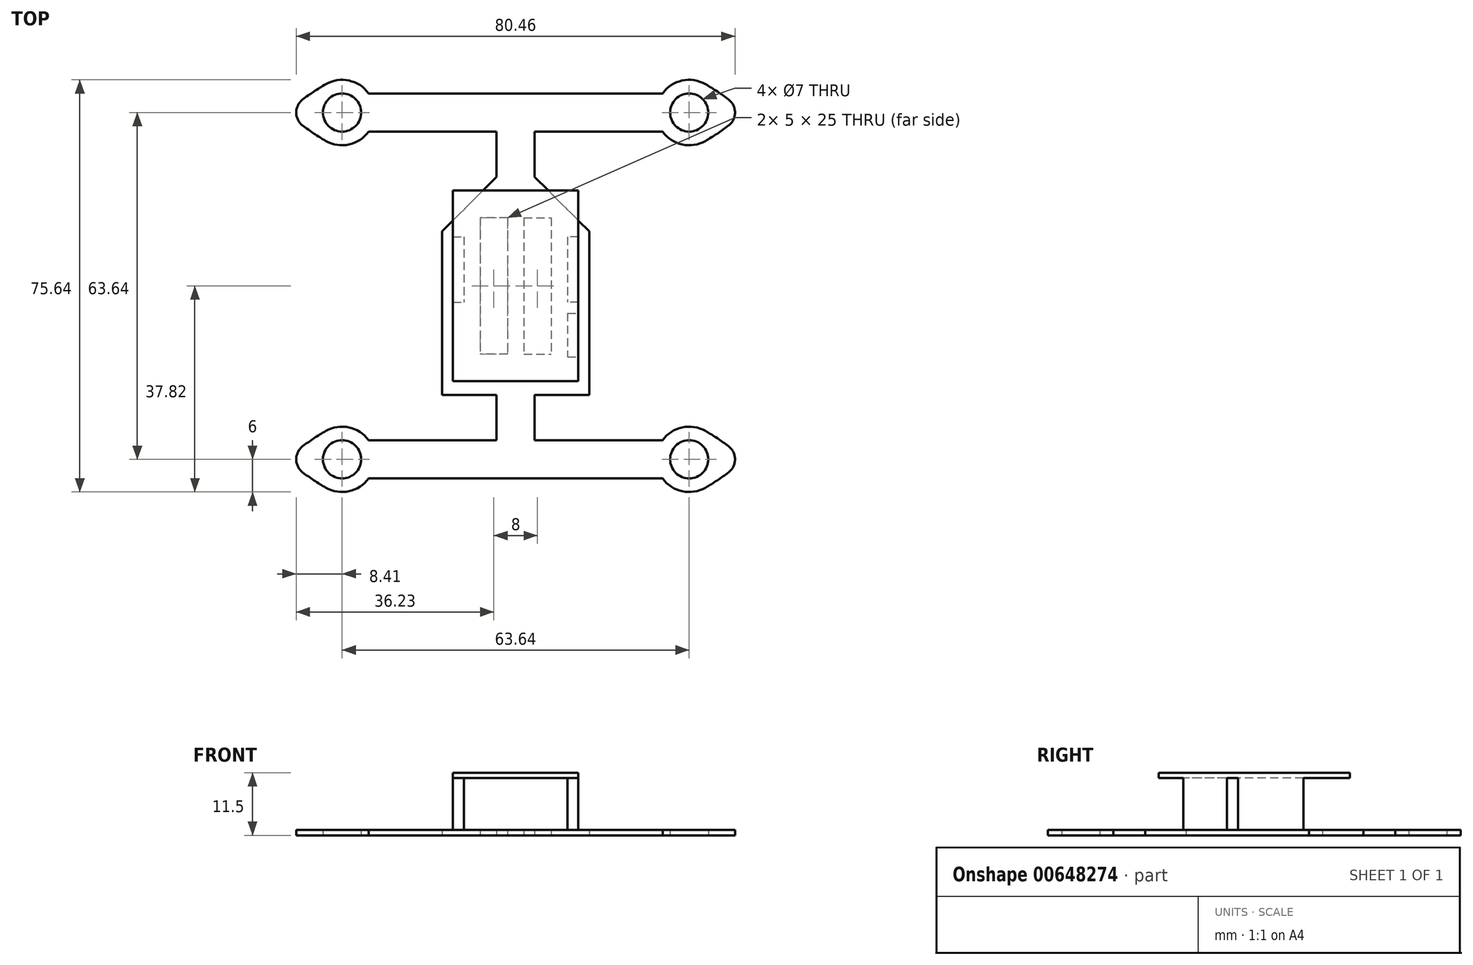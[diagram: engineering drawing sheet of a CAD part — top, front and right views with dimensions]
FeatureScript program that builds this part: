
annotation { "Feature Type Name" : "Feature", "Feature Type Description" : "" }
export const myFeature = defineFeature(function(context is Context, id is Id, definition is map)
    precondition{}
    {
        {
            var Q0;
            Q0=qCreatedBy(makeId("Top.planeOp"),FACE);
            var sketch = newSketch(context, id + "F0", { "sketchPlane" : qUnion([Q0])});
            skLineSegment(sketch, "E0.bottom", {"start": v(31.82, -31.82) * mm, "end": v(-31.82, -31.82) * mm, "construction": true});
            skLineSegment(sketch, "E0.top", {"start": v(31.82, 31.82) * mm, "end": v(-31.82, 31.82) * mm, "construction": true});
            skLineSegment(sketch, "E0.left", {"start": v(31.82, -31.82) * mm, "end": v(31.82, 31.82) * mm, "construction": true});
            skLineSegment(sketch, "E0.right", {"start": v(-31.82, -31.82) * mm, "end": v(-31.82, 31.82) * mm, "construction": true});
            skCircle(sketch, "E1", {"center": v(-31.82, 31.82) * mm, "radius": 3.5 * mm});
            skCircle(sketch, "E2", {"center": v(31.82, 31.82) * mm, "radius": 3.5 * mm});
            skCircle(sketch, "E3", {"center": v(31.82, -31.82) * mm, "radius": 3.5 * mm});
            skCircle(sketch, "E4", {"center": v(-31.82, -31.82) * mm, "radius": 3.5 * mm});
            skCircle(sketch, "E5", {"center": v(-31.82, 31.82) * mm, "radius": 6 * mm});
            skCircle(sketch, "E6", {"center": v(31.82, 31.82) * mm, "radius": 6 * mm});
            skCircle(sketch, "E7", {"center": v(31.82, -31.82) * mm, "radius": 6 * mm});
            skCircle(sketch, "E8", {"center": v(-31.82, -31.82) * mm, "radius": 6 * mm});
            skLineSegment(sketch, "E9", {"start": v(-26.95, 35.32) * mm, "end": v(26.95, 35.32) * mm});
            skLineSegment(sketch, "E10.0", {"start": v(-26.95, 28.32) * mm, "end": v(-3.5, 28.32) * mm});
            skLineSegment(sketch, "E11.0", {"start": v(3.5, 20) * mm, "end": v(3.5, 28.32) * mm});
            skLineSegment(sketch, "E12.0", {"start": v(-3.5, 20) * mm, "end": v(-3.5, 28.32) * mm});
            skLineSegment(sketch, "E13", {"start": v(3.5, 28.32) * mm, "end": v(26.95, 28.32) * mm});
            skLineSegment(sketch, "E14.MirrorCS", {"start": v(3.5, -20) * mm, "end": v(3.5, -28.32) * mm});
            skLineSegment(sketch, "E15.MirrorCS", {"start": v(-3.5, -20) * mm, "end": v(-3.5, -28.32) * mm});
            skLineSegment(sketch, "E16.MirrorCS", {"start": v(3.5, -28.32) * mm, "end": v(26.95, -28.32) * mm});
            skLineSegment(sketch, "E17.MirrorCS", {"start": v(-26.95, -35.32) * mm, "end": v(26.95, -35.32) * mm});
            skLineSegment(sketch, "E18.MirrorCS", {"start": v(-26.95, -28.32) * mm, "end": v(-3.5, -28.32) * mm});
            skArc(sketch, "E19", {"start": v(39.04, 34.2) * mm, "mid": v(36.98, 35.68) * mm, "end": v(34.82, 37.02) * mm});
            skArc(sketch, "E20", {"start": v(34.82, 26.62) * mm, "mid": v(36.98, 27.96) * mm, "end": v(39.04, 29.43) * mm});
            skPoint(sketch, "E21.visualSharp", {"position": v(41.9, 31.82) * mm});
            skArc(sketch, "E21.filletArc", {"start": v(39.04, 29.43) * mm, "mid": v(40.23, 31.82) * mm, "end": v(39.04, 34.2) * mm});
            skArc(sketch, "E22.MirrorCS", {"start": v(-34.82, 26.62) * mm, "mid": v(-36.98, 27.96) * mm, "end": v(-39.04, 29.43) * mm});
            skArc(sketch, "E23.MirrorCS", {"start": v(-39.04, 29.43) * mm, "mid": v(-40.23, 31.82) * mm, "end": v(-39.04, 34.2) * mm});
            skArc(sketch, "E24.MirrorCS", {"start": v(-39.04, 34.2) * mm, "mid": v(-36.98, 35.68) * mm, "end": v(-34.82, 37.02) * mm});
            skArc(sketch, "E25.MirrorCS", {"start": v(-34.82, -26.62) * mm, "mid": v(-36.98, -27.96) * mm, "end": v(-39.04, -29.43) * mm});
            skArc(sketch, "E26.MirrorCS", {"start": v(-39.04, -29.43) * mm, "mid": v(-40.23, -31.82) * mm, "end": v(-39.04, -34.2) * mm});
            skArc(sketch, "E27.MirrorCS", {"start": v(-39.04, -34.2) * mm, "mid": v(-36.98, -35.68) * mm, "end": v(-34.82, -37.02) * mm});
            skArc(sketch, "E28.MirrorCS", {"start": v(34.82, -26.62) * mm, "mid": v(36.98, -27.96) * mm, "end": v(39.04, -29.43) * mm});
            skArc(sketch, "E29.MirrorCS", {"start": v(39.04, -29.43) * mm, "mid": v(40.23, -31.82) * mm, "end": v(39.04, -34.2) * mm});
            skArc(sketch, "E30.MirrorCS", {"start": v(39.04, -34.2) * mm, "mid": v(36.98, -35.68) * mm, "end": v(34.82, -37.02) * mm});
            skLineSegment(sketch, "E31", {"start": v(0, 75.71) * mm, "end": v(0, -73.85) * mm, "construction": true});
            skLineSegment(sketch, "E32", {"start": v(-74.14, 0) * mm, "end": v(71.7, 0) * mm, "construction": true});
            skLineSegment(sketch, "E33.bottom", {"start": v(1.5, 12.5) * mm, "end": v(6.5, 12.5) * mm});
            skLineSegment(sketch, "E33.top", {"start": v(1.5, -12.5) * mm, "end": v(6.5, -12.5) * mm});
            skLineSegment(sketch, "E33.left", {"start": v(1.5, 12.5) * mm, "end": v(1.5, -12.5) * mm});
            skLineSegment(sketch, "E33.right", {"start": v(6.5, 12.5) * mm, "end": v(6.5, -12.5) * mm});
            skLineSegment(sketch, "E34.MirrorCS", {"start": v(-1.5, -12.5) * mm, "end": v(-6.5, -12.5) * mm});
            skLineSegment(sketch, "E35.MirrorCS", {"start": v(-1.5, 12.5) * mm, "end": v(-1.5, -12.5) * mm});
            skLineSegment(sketch, "E36.MirrorCS", {"start": v(-6.5, 12.5) * mm, "end": v(-6.5, -12.5) * mm});
            skLineSegment(sketch, "E37.MirrorCS", {"start": v(-1.5, 12.5) * mm, "end": v(-6.5, 12.5) * mm});
            skLineSegment(sketch, "E38", {"start": v(-3.5, 20) * mm, "end": v(-13.5, 10) * mm});
            skLineSegment(sketch, "E39", {"start": v(-13.5, 10) * mm, "end": v(-13.5, -20) * mm});
            skLineSegment(sketch, "E40.MirrorCS", {"start": v(3.5, 20) * mm, "end": v(13.5, 10) * mm});
            skLineSegment(sketch, "E41", {"start": v(13.5, 10) * mm, "end": v(13.5, -20) * mm});
            skLineSegment(sketch, "E42.trimOffspring", {"start": v(-3.5, -20) * mm, "end": v(-13.5, -20) * mm});
            skLineSegment(sketch, "E43", {"start": v(13.5, -20) * mm, "end": v(3.5, -20) * mm});
            skSolve(sketch);
        }
        {
            var Q0;
            Q0 = qSketchRegion(id + "F0", true);
            extrude(context, id + "F1", {"entities" : qUnion([Q0]), "depth" : 1 * mm, "offsetDistance" : 25 * mm});
        }
        {
            var Q0;
            Q0=makeQuery(id+"F1.opExtrude","CAP_FACE",FACE,{"disambiguationData":[OSD([sQuery(id+"F0.wireOp",EDGE,"E1"),sQuery(id+"F0.wireOp",EDGE,"E2"),sQuery(id+"F0.wireOp",EDGE,"E3"),sQuery(id+"F0.wireOp",EDGE,"E4"),sQuery(id+"F0.wireOp",EDGE,"E5"),sQuery(id+"F0.wireOp",EDGE,"E6"),sQuery(id+"F0.wireOp",EDGE,"E7"),sQuery(id+"F0.wireOp",EDGE,"E8"),sQuery(id+"F0.wireOp",EDGE,"E9"),sQuery(id+"F0.wireOp",EDGE,"E10.0"),sQuery(id+"F0.wireOp",EDGE,"E11.0"),sQuery(id+"F0.wireOp",EDGE,"E12.0"),sQuery(id+"F0.wireOp",EDGE,"E13"),sQuery(id+"F0.wireOp",EDGE,"E14.MirrorCS"),sQuery(id+"F0.wireOp",EDGE,"E15.MirrorCS"),sQuery(id+"F0.wireOp",EDGE,"E16.MirrorCS"),sQuery(id+"F0.wireOp",EDGE,"E17.MirrorCS"),sQuery(id+"F0.wireOp",EDGE,"E18.MirrorCS"),sQuery(id+"F0.wireOp",EDGE,"E19"),sQuery(id+"F0.wireOp",EDGE,"E20"),sQuery(id+"F0.wireOp",EDGE,"E21.filletArc"),sQuery(id+"F0.wireOp",EDGE,"E22.MirrorCS"),sQuery(id+"F0.wireOp",EDGE,"E24.MirrorCS"),sQuery(id+"F0.wireOp",EDGE,"E23.MirrorCS"),sQuery(id+"F0.wireOp",EDGE,"E25.MirrorCS"),sQuery(id+"F0.wireOp",EDGE,"E26.MirrorCS"),sQuery(id+"F0.wireOp",EDGE,"E27.MirrorCS"),sQuery(id+"F0.wireOp",EDGE,"E28.MirrorCS"),sQuery(id+"F0.wireOp",EDGE,"E29.MirrorCS"),sQuery(id+"F0.wireOp",EDGE,"E30.MirrorCS"),sQuery(id+"F0.wireOp",EDGE,"E33.bottom"),sQuery(id+"F0.wireOp",EDGE,"E33.top"),sQuery(id+"F0.wireOp",EDGE,"E33.left"),sQuery(id+"F0.wireOp",EDGE,"E33.right"),sQuery(id+"F0.wireOp",EDGE,"E34.MirrorCS"),sQuery(id+"F0.wireOp",EDGE,"E35.MirrorCS"),sQuery(id+"F0.wireOp",EDGE,"E36.MirrorCS"),sQuery(id+"F0.wireOp",EDGE,"E37.MirrorCS"),sQuery(id+"F0.wireOp",EDGE,"E38"),sQuery(id+"F0.wireOp",EDGE,"E39"),sQuery(id+"F0.wireOp",EDGE,"E40.MirrorCS"),sQuery(id+"F0.wireOp",EDGE,"E41"),sQuery(id+"F0.wireOp",EDGE,"E42.trimOffspring"),sQuery(id+"F0.wireOp",EDGE,"E43")])],"isStart":false});
            var sketch = newSketch(context, id + "F2", { "sketchPlane" : qUnion([Q0])});
            skPoint(sketch, "E44.middle", {"position": v(0, 0) * mm});
            skLineSegment(sketch, "E45", {"start": v(0, 23.55) * mm, "end": v(0, 0) * mm, "construction": true});
            skLineSegment(sketch, "E46", {"start": v(13.5, -20) * mm, "end": v(13.5, 9) * mm});
            skLineSegment(sketch, "E47.bottom", {"start": v(11.5, 9) * mm, "end": v(9.5, 9) * mm});
            skLineSegment(sketch, "E47.top", {"start": v(11.5, -3) * mm, "end": v(9.5, -3) * mm});
            skLineSegment(sketch, "E47.left", {"start": v(11.5, 9) * mm, "end": v(11.5, -3) * mm});
            skLineSegment(sketch, "E47.right", {"start": v(9.5, 9) * mm, "end": v(9.5, -3) * mm});
            skLineSegment(sketch, "E48.bottom", {"start": v(9.5, -5) * mm, "end": v(11.5, -5) * mm});
            skLineSegment(sketch, "E48.top", {"start": v(9.5, -13) * mm, "end": v(11.5, -13) * mm});
            skLineSegment(sketch, "E48.left", {"start": v(9.5, -5) * mm, "end": v(9.5, -13) * mm});
            skLineSegment(sketch, "E48.right", {"start": v(11.5, -5) * mm, "end": v(11.5, -13) * mm});
            skLineSegment(sketch, "E49.MirrorCS", {"start": v(-11.5, -3) * mm, "end": v(-9.5, -3) * mm});
            skLineSegment(sketch, "E50.MirrorCS", {"start": v(-11.5, 9) * mm, "end": v(-11.5, -3) * mm});
            skLineSegment(sketch, "E51.MirrorCS", {"start": v(-11.5, 9) * mm, "end": v(-9.5, 9) * mm});
            skLineSegment(sketch, "E52.MirrorCS", {"start": v(-9.5, 9) * mm, "end": v(-9.5, -3) * mm});
            skSolve(sketch);
        }
        {
            var Q0;
            Q0=makeQuery(id+"F2.imprint","IMPRINT",FACE,{"disambiguationData":[TD([[makeQuery(id+"F2.imprint","IMPRINT",EDGE,{"derivedFrom":sQuery(id+"F2.wireOp",EDGE,"E49.MirrorCS")}),1.0]])]});
            var Q1;
            Q1=makeQuery(id+"F2.imprint","IMPRINT",FACE,{"disambiguationData":[TD([[makeQuery(id+"F2.imprint","IMPRINT",EDGE,{"derivedFrom":sQuery(id+"F2.wireOp",EDGE,"E47.bottom")}),1.0]])]});
            var Q2;
            Q2=makeQuery(id+"F2.imprint","IMPRINT",FACE,{"disambiguationData":[TD([[makeQuery(id+"F2.imprint","IMPRINT",EDGE,{"derivedFrom":sQuery(id+"F2.wireOp",EDGE,"E48.bottom")}),-1.0]])]});
            extrude(context, id + "F3", {"entities" : qUnion([Q0, Q1, Q2]), "operationType" : NewBodyOperationType.ADD, "depth" : 9.5 * mm, "offsetDistance" : 25 * mm});
        }
        {
            var Q0;
            Q0=makeQuery(id+"F3.opExtrude","CAP_FACE",FACE,{"disambiguationData":[OSD([sQuery(id+"F2.wireOp",EDGE,"E49.MirrorCS"),sQuery(id+"F2.wireOp",EDGE,"E50.MirrorCS"),sQuery(id+"F2.wireOp",EDGE,"E51.MirrorCS"),sQuery(id+"F2.wireOp",EDGE,"E52.MirrorCS")])],"isStart":false});
            var sketch = newSketch(context, id + "F4", { "sketchPlane" : qUnion([Q0])});
            skLineSegment(sketch, "E53.bottom", {"start": v(11.5, 17.5) * mm, "end": v(-11.5, 17.5) * mm});
            skLineSegment(sketch, "E53.top", {"start": v(11.5, -17.5) * mm, "end": v(-11.5, -17.5) * mm});
            skLineSegment(sketch, "E53.left", {"start": v(11.5, 17.5) * mm, "end": v(11.5, -17.5) * mm});
            skLineSegment(sketch, "E53.right", {"start": v(-11.5, 17.5) * mm, "end": v(-11.5, -17.5) * mm});
            skPoint(sketch, "E53.middle", {"position": v(0, 0) * mm});
            skSolve(sketch);
        }
        {
            var Q0;
            Q0 = qSketchRegion(id + "F4", true);
            extrude(context, id + "F5", {"entities" : qUnion([Q0]), "operationType" : NewBodyOperationType.ADD, "depth" : 1 * mm, "offsetDistance" : 25 * mm});
        }
    });
